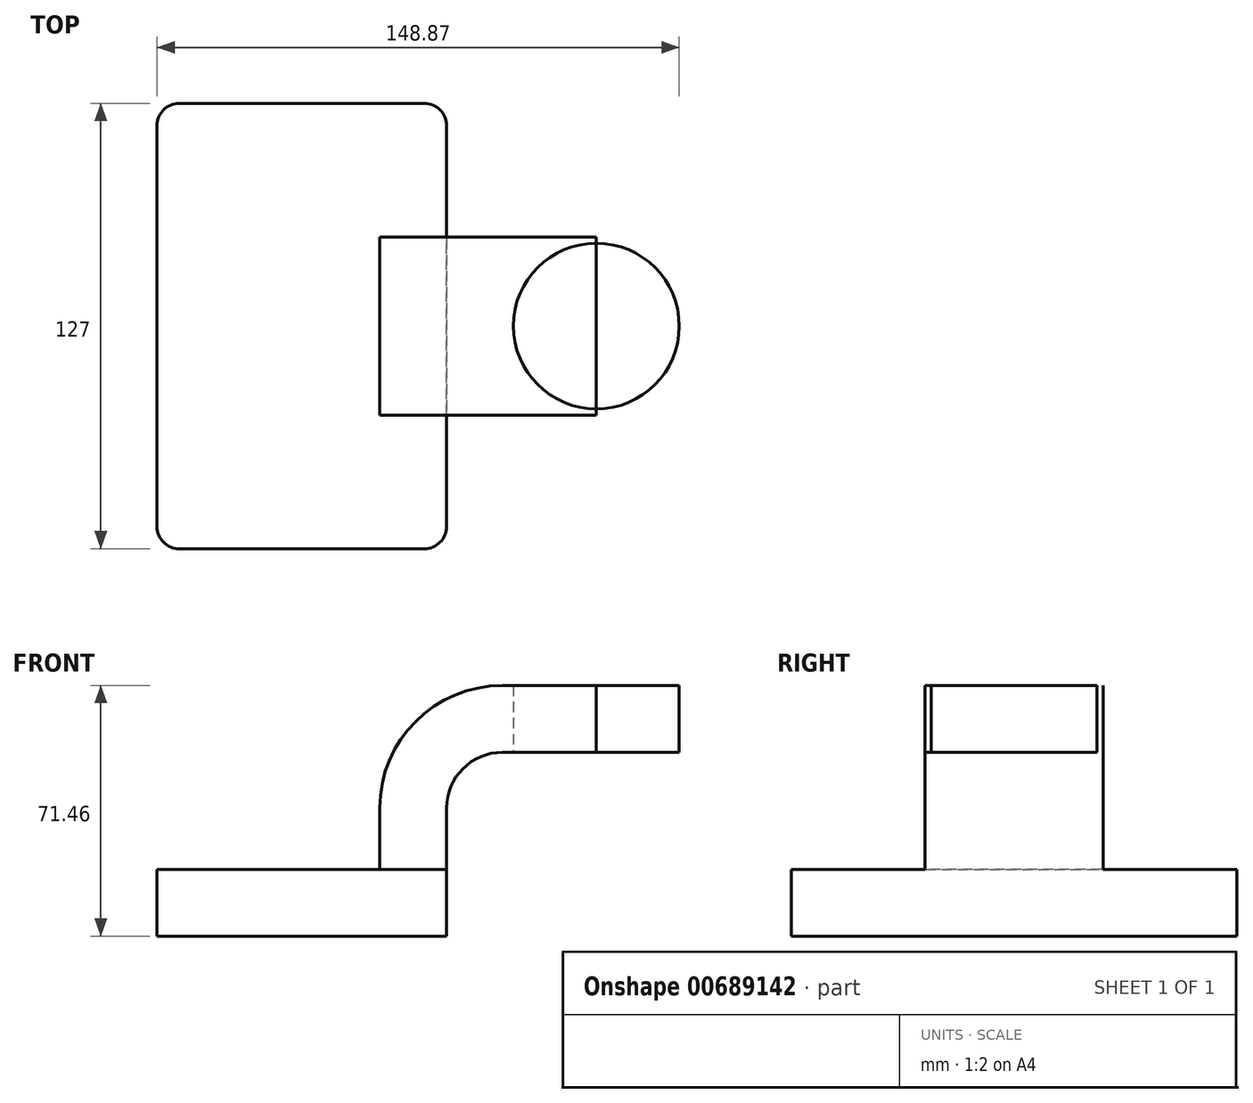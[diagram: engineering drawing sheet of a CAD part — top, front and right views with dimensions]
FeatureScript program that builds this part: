
annotation { "Feature Type Name" : "Feature", "Feature Type Description" : "" }
export const myFeature = defineFeature(function(context is Context, id is Id, definition is map)
    precondition{}
    {
        {
            var Q0;
            Q0=qCreatedBy(makeId("Front.planeOp"),FACE);
            var sketch = newSketch(context, id + "F0", { "sketchPlane" : qUnion([Q0])});
            skLineSegment(sketch, "E0.bottom", {"start": v(41.27, 9.53) * mm, "end": v(-41.28, 9.53) * mm});
            skLineSegment(sketch, "E0.top", {"start": v(41.28, -9.52) * mm, "end": v(-41.27, -9.52) * mm});
            skLineSegment(sketch, "E0.left", {"start": v(41.28, 9.53) * mm, "end": v(41.28, -9.52) * mm});
            skLineSegment(sketch, "E0.right", {"start": v(-41.28, 9.53) * mm, "end": v(-41.27, -9.52) * mm});
            skPoint(sketch, "E0.middle", {"position": v(0, 0) * mm});
            skLineSegment(sketch, "E1.bottom", {"start": v(111.12, 66.68) * mm, "end": v(60.32, 66.68) * mm});
            skLineSegment(sketch, "E1.top", {"start": v(111.13, 38.1) * mm, "end": v(60.32, 38.1) * mm});
            skLineSegment(sketch, "E1.left", {"start": v(111.12, 66.68) * mm, "end": v(111.13, 38.1) * mm});
            skLineSegment(sketch, "E1.right", {"start": v(60.32, 66.68) * mm, "end": v(60.32, 38.1) * mm});
            skPoint(sketch, "E1.middle", {"position": v(85.72, 52.39) * mm});
            skLineSegment(sketch, "E2", {"start": v(41.27, 9.53) * mm, "end": v(41.27, 26.97) * mm});
            skArc(sketch, "E3", {"start": v(41.27, 26.97) * mm, "mid": v(45.93, 38.22) * mm, "end": v(57.18, 42.88) * mm});
            skLineSegment(sketch, "E4", {"start": v(57.18, 42.88) * mm, "end": v(83.96, 42.88) * mm});
            skLineSegment(sketch, "E5.0", {"start": v(57.18, 61.93) * mm, "end": v(83.96, 61.93) * mm});
            skArc(sketch, "E5.1", {"start": v(22.22, 26.97) * mm, "mid": v(32.46, 51.69) * mm, "end": v(57.18, 61.93) * mm});
            skLineSegment(sketch, "E5.2", {"start": v(22.22, 9.53) * mm, "end": v(22.22, 26.97) * mm});
            skLineSegment(sketch, "E6", {"start": v(83.96, 42.88) * mm, "end": v(83.96, 61.93) * mm});
            skFitSpline(sketch, "E7", {"points": [v(-41.28, 9.52) * mm, v(57.18, 61.93) * mm], "startDerivative": vector(11.6, 121.09) * mm, "endDerivative": vector(139.3, -30.96) * mm});
            skSolve(sketch);
        }
        {
            var Q0;
            Q0=makeQuery(id+"F0.imprint","IMPRINT",FACE,{"disambiguationData":[TD([[makeQuery(id+"F0.imprint","IMPRINT",EDGE,{"derivedFrom":sQuery(id+"F0.wireOp",EDGE,"E0.top")}),-1.0]])]});
            extrude(context, id + "F1", {"entities" : qUnion([Q0]), "endBound" : BoundingType.SYMMETRIC, "oppositeDirection" : true, "depth" : 127 * mm, "offsetDistance" : 25.4 * mm});
        }
        {
            var Q0;
            {var subQ1=sQuery(id+"F0.wireOp",EDGE,"E2");Q0=makeQuery(id+"F0.imprint","IMPRINT",FACE,{"disambiguationData":[TD([[makeQuery(id+"F0.imprint","IMPRINT",EDGE,{"derivedFrom":subQ1}),1.0]])]});}
            var Q1;
            {var subQ5=sQuery(id+"F0.wireOp",EDGE,"E6");Q1=makeQuery(id+"F0.imprint","IMPRINT",FACE,{"disambiguationData":[TD([[makeQuery(id+"F0.imprint","IMPRINT",EDGE,{"derivedFrom":subQ5}),1.0]])]});}
            extrude(context, id + "F2", {"entities" : qUnion([Q0, Q1]), "operationType" : NewBodyOperationType.ADD, "endBound" : BoundingType.SYMMETRIC, "depth" : 50.8 * mm, "offsetDistance" : 25.4 * mm});
        }
        {
            var Q0;
            Q0=makeQuery(id+"F0.imprint","IMPRINT",FACE,{"disambiguationData":[TD([[makeQuery(id+"F0.imprint","IMPRINT",EDGE,{"derivedFrom":sQuery(id+"F0.wireOp",EDGE,"E5.1")}),1.0]])]});
            extrude(context, id + "F3", {"entities" : qUnion([Q0]), "operationType" : NewBodyOperationType.ADD, "endBound" : BoundingType.SYMMETRIC, "depth" : 15.88 * mm, "offsetDistance" : 25.4 * mm});
        }
        {
            var Q0;
            {var subQ5=sQuery(id+"F0.wireOp",EDGE,"E6");Q0=makeQuery(id+"F0.imprint","IMPRINT",FACE,{"disambiguationData":[TD([[makeQuery(id+"F0.imprint","IMPRINT",EDGE,{"derivedFrom":subQ5}),1.0]])]});}
            var Q1;
            Q1=sQuery(id+"F0.wireOp",EDGE,"E6");
            revolve(context, id + "F4", {"entities" : qUnion([Q0]), "axis" : qUnion([Q1]), "revolveType" : RevolveType.FULL});
        }
        {
            var Q0;
            Q0=makeQuery(id+"F1.opExtrude","CAP_EDGE",EDGE,{"disambiguationData":[OSD([sQuery(id+"F0.wireOp",EDGE,"E0.right")])],"isStart":true});
            var Q1;
            Q1=makeQuery(id+"F1.opExtrude","CAP_EDGE",EDGE,{"disambiguationData":[OSD([sQuery(id+"F0.wireOp",EDGE,"E0.left")])],"isStart":true});
            var Q2;
            Q2=makeQuery(id+"F1.opExtrude","CAP_EDGE",EDGE,{"disambiguationData":[OSD([sQuery(id+"F0.wireOp",EDGE,"E0.right")])],"isStart":false});
            var Q3;
            Q3=makeQuery(id+"F1.opExtrude","CAP_EDGE",EDGE,{"disambiguationData":[OSD([sQuery(id+"F0.wireOp",EDGE,"E0.left")])],"isStart":false});
            fillet(context, id + "F5", {"entities" : qUnion([Q0, Q1, Q2, Q3]), "radius" : 6.35 * mm, "tangentPropagation" : true, "allowEdgeOverflow" : false});
        }
    });
